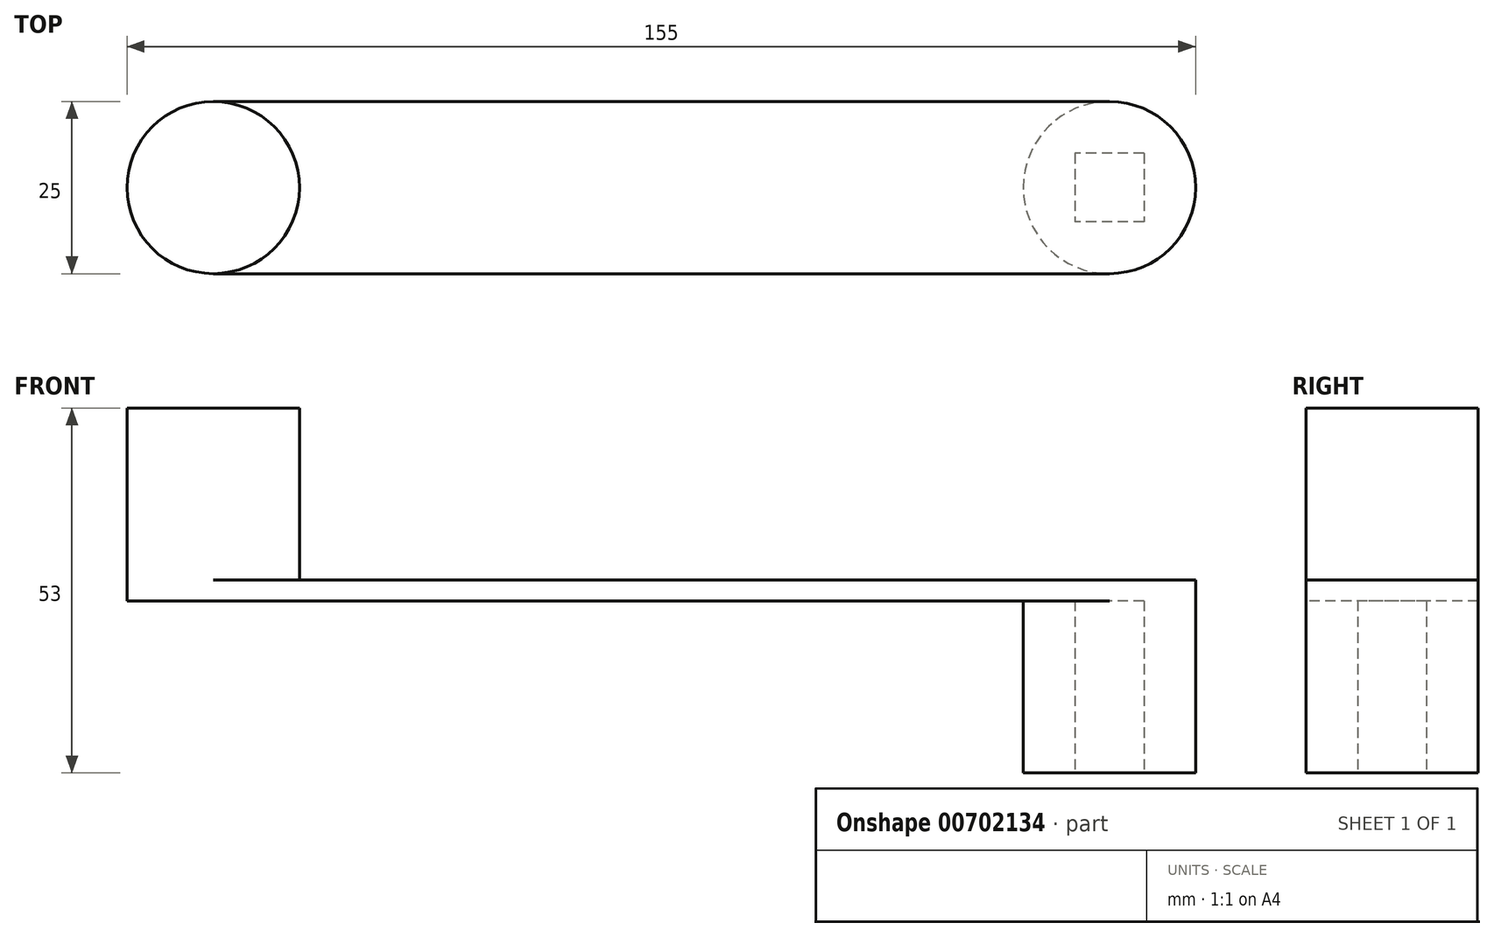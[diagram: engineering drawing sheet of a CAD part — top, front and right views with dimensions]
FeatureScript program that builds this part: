
annotation { "Feature Type Name" : "Feature", "Feature Type Description" : "" }
export const myFeature = defineFeature(function(context is Context, id is Id, definition is map)
    precondition{}
    {
        {
            var Q0;
            Q0=qCreatedBy(makeId("Top.planeOp"),FACE);
            var sketch = newSketch(context, id + "F0", { "sketchPlane" : qUnion([Q0])});
            skCircle(sketch, "E0", {"center": v(0, 0) * mm, "radius": 12.5 * mm});
            skLineSegment(sketch, "E1.bottom", {"start": v(5, 5) * mm, "end": v(-5, 5) * mm});
            skLineSegment(sketch, "E1.top", {"start": v(5, -5) * mm, "end": v(-5, -5) * mm});
            skLineSegment(sketch, "E1.left", {"start": v(5, 5) * mm, "end": v(5, -5) * mm});
            skLineSegment(sketch, "E1.right", {"start": v(-5, 5) * mm, "end": v(-5, -5) * mm});
            skSolve(sketch);
        }
        {
            var Q0;
            Q0=makeQuery(id+"F0.imprint","IMPRINT",FACE,{"disambiguationData":[TD([[makeQuery(id+"F0.imprint","IMPRINT",EDGE,{"derivedFrom":sQuery(id+"F0.wireOp",EDGE,"E0")}),1.0]])]});
            extrude(context, id + "F1", {"entities" : qUnion([Q0]), "depth" : 25 * mm, "offsetDistance" : 25 * mm});
        }
        {
            var Q0;
            Q0=makeQuery(id+"F1.opExtrude","CAP_FACE",FACE,{"disambiguationData":[OSD([sQuery(id+"F0.wireOp",EDGE,"E0"),sQuery(id+"F0.wireOp",EDGE,"E1.bottom"),sQuery(id+"F0.wireOp",EDGE,"E1.top"),sQuery(id+"F0.wireOp",EDGE,"E1.left"),sQuery(id+"F0.wireOp",EDGE,"E1.right")])],"isStart":false});
            var sketch = newSketch(context, id + "F2", { "sketchPlane" : qUnion([Q0])});
            skArc(sketch, "E2.0", {"start": v(0, -12.5) * mm, "mid": v(12.5, 0) * mm, "end": v(0, 12.5) * mm});
            skLineSegment(sketch, "E3.0", {"start": v(0, 12.5) * mm, "end": v(-130, 12.5) * mm});
            skLineSegment(sketch, "E4.0", {"start": v(0, -12.5) * mm, "end": v(-130, -12.5) * mm});
            skArc(sketch, "E5", {"start": v(-130, 12.5) * mm, "mid": v(-142.5, 0) * mm, "end": v(-130, -12.5) * mm});
            skSolve(sketch);
        }
        {
            var Q0;
            Q0 = qSketchRegion(id + "F2", true);
            extrude(context, id + "F3", {"entities" : qUnion([Q0]), "operationType" : NewBodyOperationType.ADD, "depth" : 3 * mm, "offsetDistance" : 25 * mm});
        }
        {
            var Q0;
            Q0=makeQuery(id+"F3.opExtrude","CAP_FACE",FACE,{"disambiguationData":[OSD([sQuery(id+"F2.wireOp",EDGE,"E2.0"),sQuery(id+"F2.wireOp",EDGE,"E3.0"),sQuery(id+"F2.wireOp",EDGE,"E4.0"),sQuery(id+"F2.wireOp",EDGE,"E5")])],"isStart":false});
            var sketch = newSketch(context, id + "F4", { "sketchPlane" : qUnion([Q0])});
            skCircle(sketch, "E6", {"center": v(-130, 0) * mm, "radius": 12.5 * mm});
            skSolve(sketch);
        }
        {
            var Q0;
            {var subQ0=sQuery(id+"F4.wireOp",EDGE,"E6");var subQ1=makeQuery(id+"F4.imprint","INTERSECT",VERTEX,{"derivedFrom":[makeQuery(id+"F3.opExtrude","CAP_EDGE",EDGE,{"disambiguationData":[OSD([sQuery(id+"F2.wireOp",EDGE,"E3.0")])],"isStart":false}),subQ0]});Q0=makeQuery(id+"F4.imprint","IMPRINT",FACE,{"disambiguationData":[TD([[makeQuery(id+"F4.imprint","IMPRINT",EDGE,{"disambiguationData":[TD([[subQ1,-1.0]])],"derivedFrom":subQ0}),1.0]])]});}
            extrude(context, id + "F5", {"entities" : qUnion([Q0]), "operationType" : NewBodyOperationType.ADD, "depth" : 25 * mm, "offsetDistance" : 25 * mm});
        }
    });
